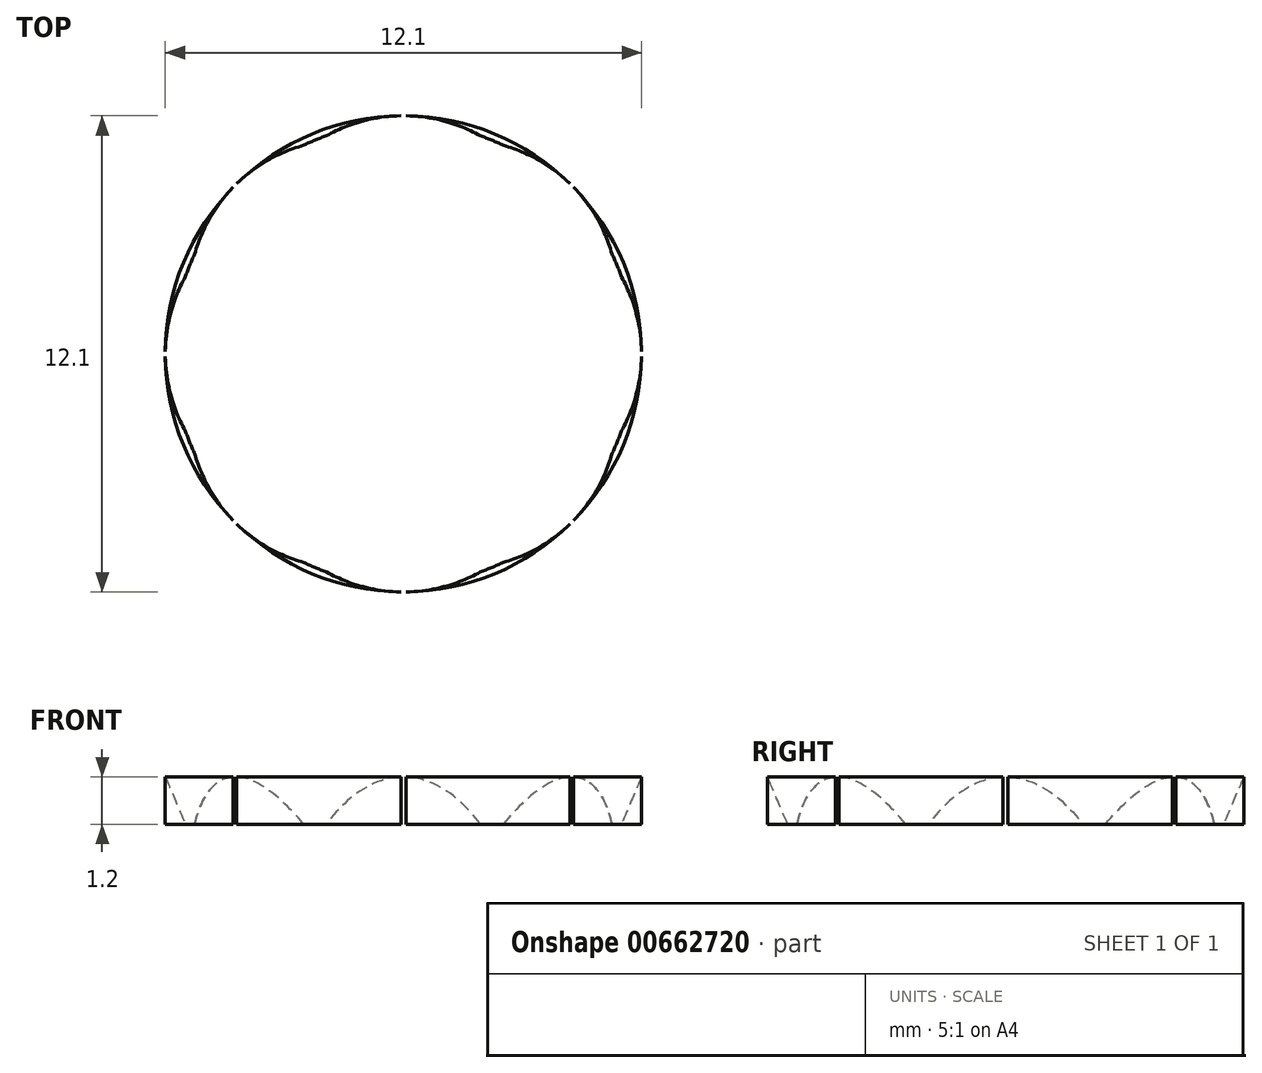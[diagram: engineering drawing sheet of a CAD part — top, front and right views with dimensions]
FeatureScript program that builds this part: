
annotation { "Feature Type Name" : "Feature", "Feature Type Description" : "" }
export const myFeature = defineFeature(function(context is Context, id is Id, definition is map)
    precondition{}
    {
        {
            var Q0;
            Q0=qCreatedBy(makeId("Top.planeOp"),FACE);
            var sketch = newSketch(context, id + "F0", { "sketchPlane" : qUnion([Q0])});
            skCircle(sketch, "E0", {"center": v(0, 0) * mm, "radius": 6.05 * mm});
            skPoint(sketch, "E1", {"position": v(6.05, 0) * mm});
            skPoint(sketch, "E2", {"position": v(5.88, 0) * mm});
            skSolve(sketch);
        }
        {
            var Q0;
            Q0=qCreatedBy(makeId("Front.planeOp"),FACE);
            var sketch = newSketch(context, id + "F1", { "sketchPlane" : qUnion([Q0])});
            skLineSegment(sketch, "E3", {"start": v(5.87, 0) * mm, "end": v(6.05, 0) * mm});
            skLineSegment(sketch, "E4", {"start": v(6.05, 0) * mm, "end": v(6.05, 1.2) * mm});
            skLineSegment(sketch, "E5", {"start": v(6.05, 1.2) * mm, "end": v(5.87, 0) * mm});
            skSolve(sketch);
        }
        {
            var Q0;
            Q0=makeQuery(id+"F1.imprint","IMPRINT",FACE,{"disambiguationData":[TD([[makeQuery(id+"F1.imprint","IMPRINT",EDGE,{"derivedFrom":sQuery(id+"F1.wireOp",EDGE,"E3")}),1.0]])]});
            var Q1;
            Q1=sQuery(id+"F0.wireOp",EDGE,"E0");
            revolve(context, id + "F2", {"entities" : qUnion([Q0]), "axis" : qUnion([Q1]), "revolveType" : RevolveType.FULL});
        }
        {
            var Q0;
            Q0=qCreatedBy(makeId("Top.planeOp"),FACE);
            var sketch = newSketch(context, id + "F3", { "sketchPlane" : qUnion([Q0])});
            skCircle(sketch, "E6", {"center": v(0, 2.05) * mm, "radius": 4 * mm});
            skSolve(sketch);
        }
        {
            var Q0;
            Q0=makeQuery(id+"F3.imprint","IMPRINT",FACE,{"disambiguationData":[TD([[makeQuery(id+"F3.imprint","IMPRINT",EDGE,{"derivedFrom":sQuery(id+"F3.wireOp",EDGE,"E6")}),1.0]])]});
            extrude(context, id + "F4", {"entities" : qUnion([Q0]), "depth" : 1.2 * mm, "offsetDistance" : 25 * mm});
        }
        {
            var Q0;
            Q0=makeQuery(id+"F4.opExtrude","SWEPT_BODY",BODY,{"disambiguationData":[OSD([sQuery(id+"F3.wireOp",EDGE,"E6")])]});
            var Q1;
            Q1=makeQuery(id+"F2.opRevolve","SWEPT_EDGE",EDGE,{"disambiguationData":[OSD([sQuery(id+"F1.wireOp",EDGE,"E3"),sQuery(id+"F1.wireOp",EDGE,"E4")])]});
            circularPattern(context, id + "F5", {"operationType" : NewBodyOperationType.REMOVE, "entities" : qUnion([Q0]), "axis" : qUnion([Q1]), "angle" : 360 * degree, "instanceCount" : 8, "equalSpace" : true});
        }
    });
